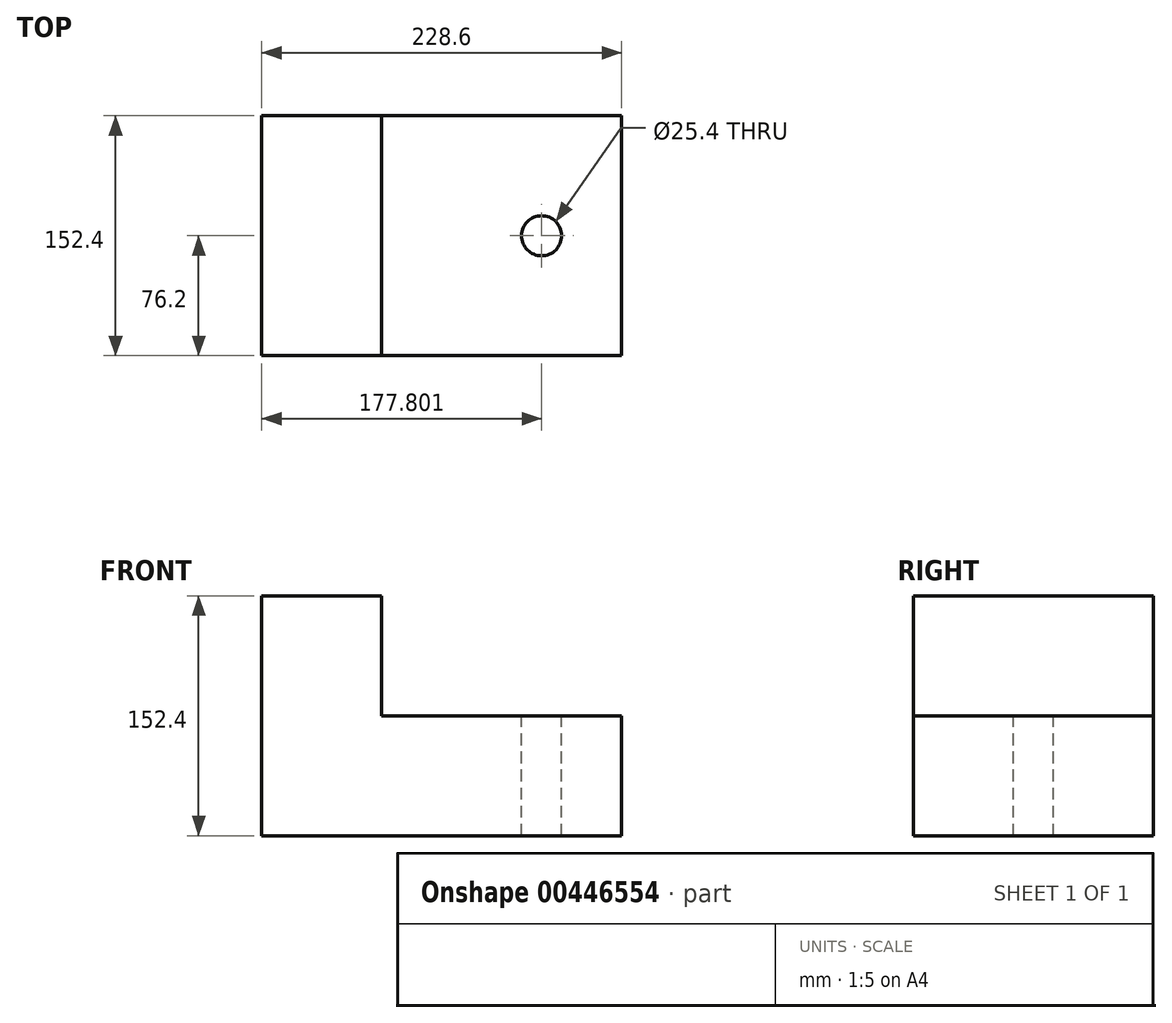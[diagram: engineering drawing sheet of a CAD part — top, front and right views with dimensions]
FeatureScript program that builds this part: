
annotation { "Feature Type Name" : "Feature", "Feature Type Description" : "" }
export const myFeature = defineFeature(function(context is Context, id is Id, definition is map)
    precondition{}
    {
        {
            var Q0;
            Q0=qCreatedBy(makeId("Front.planeOp"),FACE);
            var sketch = newSketch(context, id + "F0", { "sketchPlane" : qUnion([Q0])});
            skLineSegment(sketch, "E0.bottom", {"start": v(-108.2, 76.2) * mm, "end": v(120.4, 76.2) * mm});
            skLineSegment(sketch, "E0.top", {"start": v(-108.2, -76.2) * mm, "end": v(120.4, -76.2) * mm});
            skLineSegment(sketch, "E0.left", {"start": v(-108.2, 76.2) * mm, "end": v(-108.2, -76.2) * mm});
            skLineSegment(sketch, "E0.right", {"start": v(120.4, 76.2) * mm, "end": v(120.4, -76.2) * mm});
            skSolve(sketch);
        }
        {
            var Q0;
            Q0=makeQuery(id+"F0.imprint","IMPRINT",FACE,{"disambiguationData":[TD([[makeQuery(id+"F0.imprint","IMPRINT",EDGE,{"derivedFrom":sQuery(id+"F0.wireOp",EDGE,"E0.bottom")}),-1.0]])]});
            extrude(context, id + "F1", {"entities" : qUnion([Q0]), "endBound" : BoundingType.SYMMETRIC, "depth" : 152.4 * mm});
        }
        {
            var Q0;
            Q0=makeQuery(id+"F1.opExtrude","CAP_FACE",FACE,{"disambiguationData":[OSD([sQuery(id+"F0.wireOp",EDGE,"E0.bottom"),sQuery(id+"F0.wireOp",EDGE,"E0.top"),sQuery(id+"F0.wireOp",EDGE,"E0.left"),sQuery(id+"F0.wireOp",EDGE,"E0.right")])],"isStart":false});
            var sketch = newSketch(context, id + "F2", { "sketchPlane" : qUnion([Q0])});
            skLineSegment(sketch, "E1.bottom", {"start": v(120.4, 76.2) * mm, "end": v(-32.04, 76.2) * mm});
            skLineSegment(sketch, "E1.top", {"start": v(120.4, 0) * mm, "end": v(-32.04, 0) * mm});
            skLineSegment(sketch, "E1.left", {"start": v(120.4, 76.2) * mm, "end": v(120.4, 0) * mm});
            skLineSegment(sketch, "E1.right", {"start": v(-32.04, 76.2) * mm, "end": v(-32.04, 0) * mm});
            skSolve(sketch);
        }
        {
            var Q0;
            Q0=makeQuery(id+"F2.imprint","IMPRINT",FACE,{"disambiguationData":[TD([[makeQuery(id+"F2.imprint","IMPRINT",EDGE,{"derivedFrom":sQuery(id+"F2.wireOp",EDGE,"E1.bottom")}),-1.0]])]});
            extrude(context, id + "F3", {"entities" : qUnion([Q0]), "operationType" : NewBodyOperationType.REMOVE, "endBound" : BoundingType.THROUGH_ALL, "oppositeDirection" : true, "depth" : 25.4 * mm});
        }
        {
            var Q0;
            Q0=makeQuery(id+"F3.boolean.opBoolean","COPY",FACE,{"derivedFrom":makeQuery(id+"F3.opExtrude","SWEPT_FACE",FACE,{"disambiguationData":[OSD([sQuery(id+"F2.wireOp",EDGE,"E1.top")])]})});
            var sketch = newSketch(context, id + "F4", { "sketchPlane" : qUnion([Q0])});
            skPoint(sketch, "E2", {"position": v(69.6, 0) * mm});
            skSolve(sketch);
        }
        {
            var Q0;
            Q0=sQuery(id+"F4.wireOp",VERTEX,"E2");
            var Q1;
            Q1=makeQuery(id+"F1.opExtrude","SWEPT_BODY",BODY,{"disambiguationData":[OSD([sQuery(id+"F0.wireOp",EDGE,"E0.bottom"),sQuery(id+"F0.wireOp",EDGE,"E0.top"),sQuery(id+"F0.wireOp",EDGE,"E0.left"),sQuery(id+"F0.wireOp",EDGE,"E0.right")])]});
            hole(context, id + "F5", {"style" : HoleStyle.SIMPLE, "endStyle" : HoleEndStyle.THROUGH, "holeDiameter" : 25.4 * mm, "isTappedThrough" : true, "tappedDepth" : 12.7 * mm, "tapClearance" : 3, "locations" : qUnion([Q0]), "scope" : qUnion([Q1])});
        }
    });
